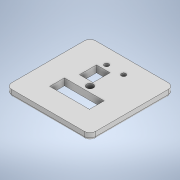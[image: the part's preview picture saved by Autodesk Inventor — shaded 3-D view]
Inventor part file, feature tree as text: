
AUTODESK INVENTOR PART (.ipt)
format: ipt  version: 2020 (Build 240168000, 168)  size: 148,480 bytes
history: native  units: in
note: dims shown in document units (in); Inventor stores cm internally (conversion verified against a paired STEP export)
features: extrude x2, fillet x2, sketch x2
ambient origin geometry x8: Origin, YZ Plane, XZ Plane, XY Plane, X Axis, Y Axis, Z Axis, Center Point
bodies: Solid1 (feature_tree)
feature tree (6):
  extrude  "Extrusion1"  Depth=2.9134in
  fillet  "Fillet1"  Radius=0.2362in
  fillet  "Fillet2"  Radius=0.1969in
  extrude  "Extrusion6"  Depth=0.2362in
  sketch  "Sketch1"  dims[d0=2.9134in d1=2.9134in d2=0.2362in d3=0.0in d4=0.1969in]
  sketch  "Sketch6"  dims[d24=0.0787in d29=0.2362in d30=0.1575in d31=0.1575in d32=0.4724in d33=0.5906in d34=1.378in d35=0.5118in d36=0.3937in d37=0.0in]
